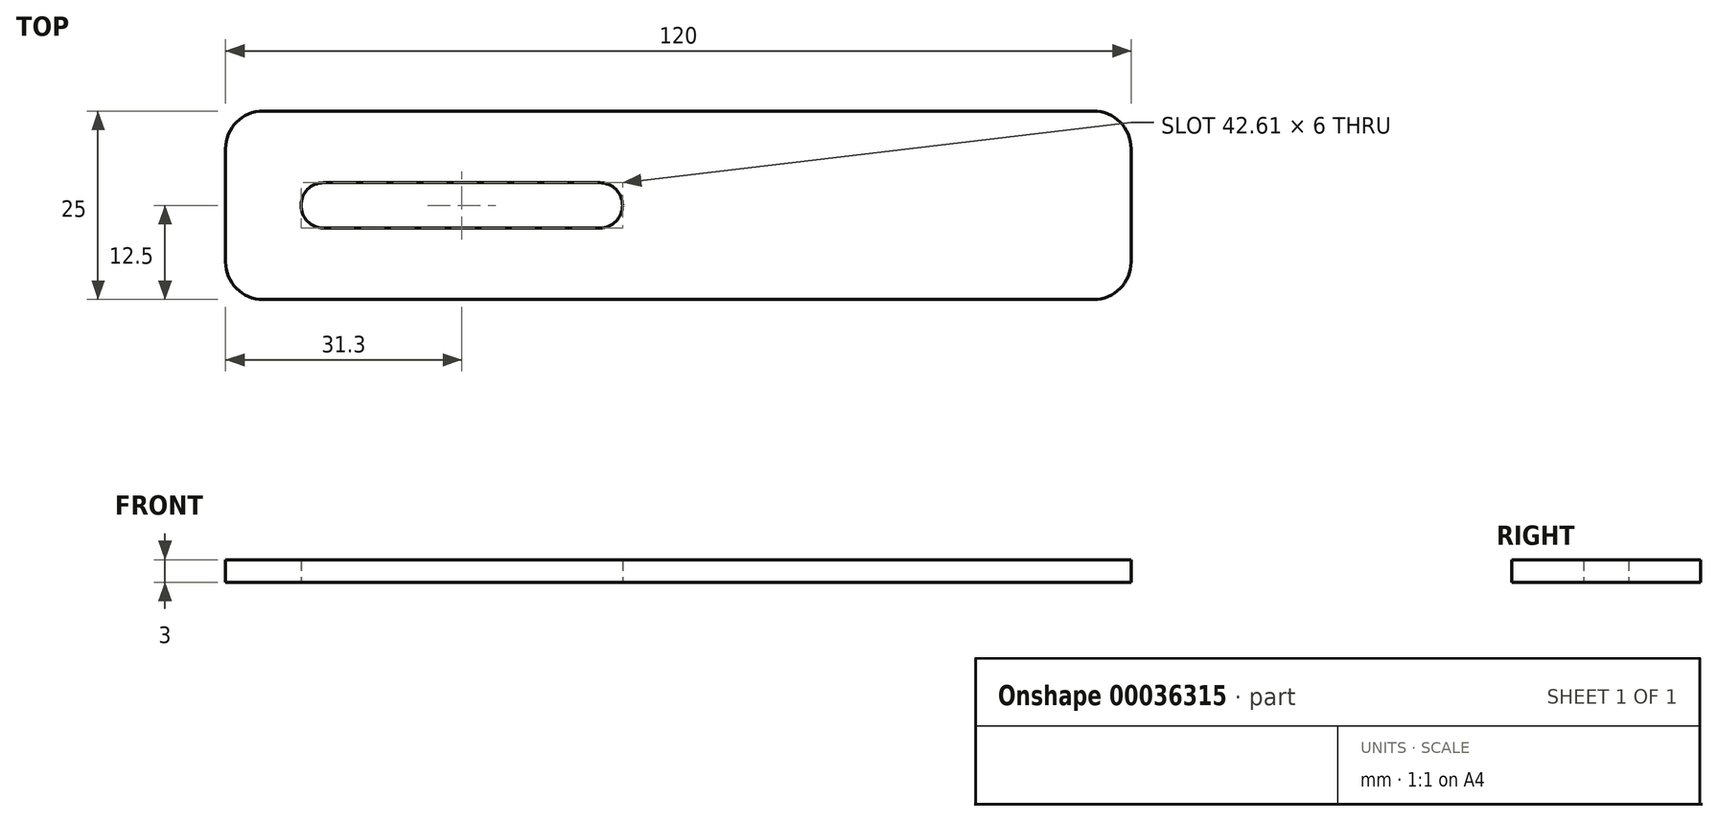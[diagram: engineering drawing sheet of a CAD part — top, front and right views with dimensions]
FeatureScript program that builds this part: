
annotation { "Feature Type Name" : "Feature", "Feature Type Description" : "" }
export const myFeature = defineFeature(function(context is Context, id is Id, definition is map)
    precondition{}
    {
        {
            var Q0;
            Q0=qCreatedBy(makeId("Top.planeOp"),FACE);
            var sketch = newSketch(context, id + "F0", { "sketchPlane" : qUnion([Q0])});
            skLineSegment(sketch, "E0.bottom", {"start": v(-38.85, 0) * mm, "end": v(81.15, 0) * mm});
            skLineSegment(sketch, "E0.top", {"start": v(-38.85, -25) * mm, "end": v(81.15, -25) * mm});
            skLineSegment(sketch, "E0.left", {"start": v(-38.85, 0) * mm, "end": v(-38.85, -25) * mm});
            skLineSegment(sketch, "E0.right", {"start": v(81.15, 0) * mm, "end": v(81.15, -25) * mm});
            skLineSegment(sketch, "E1", {"start": v(-38.85, -12.5) * mm, "end": v(81.15, -12.5) * mm, "construction": true});
            skCircle(sketch, "E2", {"center": v(-25.85, -12.5) * mm, "radius": 3 * mm});
            skLineSegment(sketch, "E3.bottom", {"start": v(81.15, 0) * mm, "end": v(56.15, 0) * mm});
            skLineSegment(sketch, "E3.top", {"start": v(81.15, 40) * mm, "end": v(56.15, 40) * mm});
            skLineSegment(sketch, "E3.left", {"start": v(81.15, 0) * mm, "end": v(81.15, 40) * mm});
            skLineSegment(sketch, "E3.right", {"start": v(56.15, 0) * mm, "end": v(56.15, 40) * mm});
            skCircle(sketch, "E4", {"center": v(10.75, -12.5) * mm, "radius": 3 * mm});
            skLineSegment(sketch, "E5.bottom", {"start": v(-25.85, -15.5) * mm, "end": v(10.75, -15.5) * mm});
            skLineSegment(sketch, "E5.top", {"start": v(-25.85, -9.5) * mm, "end": v(10.75, -9.5) * mm});
            skLineSegment(sketch, "E5.left", {"start": v(-25.85, -15.5) * mm, "end": v(-25.85, -9.5) * mm});
            skLineSegment(sketch, "E5.right", {"start": v(10.75, -15.5) * mm, "end": v(10.75, -9.5) * mm});
            skLineSegment(sketch, "E6", {"start": v(68.65, 40) * mm, "end": v(68.65, 0) * mm, "construction": true});
            skCircle(sketch, "E7", {"center": v(68.65, 28) * mm, "radius": 3 * mm});
            skCircle(sketch, "E8", {"center": v(68.65, 4.48) * mm, "radius": 3 * mm});
            skLineSegment(sketch, "E9.bottom", {"start": v(65.65, 28) * mm, "end": v(71.65, 28) * mm});
            skLineSegment(sketch, "E9.top", {"start": v(65.65, 4.48) * mm, "end": v(71.65, 4.48) * mm});
            skLineSegment(sketch, "E9.left", {"start": v(65.65, 28) * mm, "end": v(65.65, 4.48) * mm});
            skLineSegment(sketch, "E9.right", {"start": v(71.65, 28) * mm, "end": v(71.65, 4.48) * mm});
            skSolve(sketch);
        }
        {
            var Q0;
            Q0=makeQuery(id+"F0.imprint","IMPRINT",FACE,{"disambiguationData":[TD([[makeQuery(id+"F0.imprint","IMPRINT",EDGE,{"derivedFrom":sQuery(id+"F0.wireOp",EDGE,"E0.bottom")}),-1.0]])]});
            var Q1;
            Q1=makeQuery(id+"F0.imprint","IMPRINT",FACE,{"disambiguationData":[TD([[makeQuery(id+"F0.imprint","IMPRINT",EDGE,{"derivedFrom":sQuery(id+"F0.wireOp",EDGE,"E3.bottom")}),-1.0]])]});
            extrude(context, id + "F1", {"entities" : qUnion([Q0, Q1]), "depth" : 3 * mm});
        }
        {
            var Q0;
            Q0=makeQuery(id+"F1.opExtrude","SWEPT_EDGE",EDGE,{"disambiguationData":[OSD([sQuery(id+"F0.wireOp",EDGE,"E0.top"),sQuery(id+"F0.wireOp",EDGE,"E0.left")])]});
            var Q1;
            Q1=makeQuery(id+"F1.opExtrude","SWEPT_EDGE",EDGE,{"disambiguationData":[OSD([sQuery(id+"F0.wireOp",EDGE,"E0.top"),sQuery(id+"F0.wireOp",EDGE,"E0.right")])]});
            var Q2;
            Q2=makeQuery(id+"F1.opExtrude","SWEPT_EDGE",EDGE,{"disambiguationData":[OSD([sQuery(id+"F0.wireOp",EDGE,"E0.bottom"),sQuery(id+"F0.wireOp",EDGE,"E0.right")])]});
            var Q3;
            Q3=makeQuery(id+"F1.opExtrude","SWEPT_EDGE",EDGE,{"disambiguationData":[OSD([sQuery(id+"F0.wireOp",EDGE,"E0.bottom"),sQuery(id+"F0.wireOp",EDGE,"E0.left")])]});
            var Q4;
            Q4=makeQuery(id+"F1.opExtrude","SWEPT_EDGE",EDGE,{"disambiguationData":[OSD([sQuery(id+"F0.wireOp",EDGE,"E3.top"),sQuery(id+"F0.wireOp",EDGE,"E3.left")])]});
            var Q5;
            Q5=makeQuery(id+"F1.opExtrude","SWEPT_EDGE",EDGE,{"disambiguationData":[OSD([sQuery(id+"F0.wireOp",EDGE,"E3.top"),sQuery(id+"F0.wireOp",EDGE,"E3.right")])]});
            var Q6;
            Q6=makeQuery(id+"F1.opExtrude","SWEPT_EDGE",EDGE,{"disambiguationData":[OSD([sQuery(id+"F0.wireOp",EDGE,"E0.bottom"),sQuery(id+"F0.wireOp",EDGE,"E3.bottom"),sQuery(id+"F0.wireOp",EDGE,"E3.right")])]});
            fillet(context, id + "F2", {"entities" : qUnion([Q0, Q1, Q2, Q3, Q4, Q5, Q6]), "radius" : 5 * mm, "tangentPropagation" : true, "allowEdgeOverflow" : false});
        }
    });
